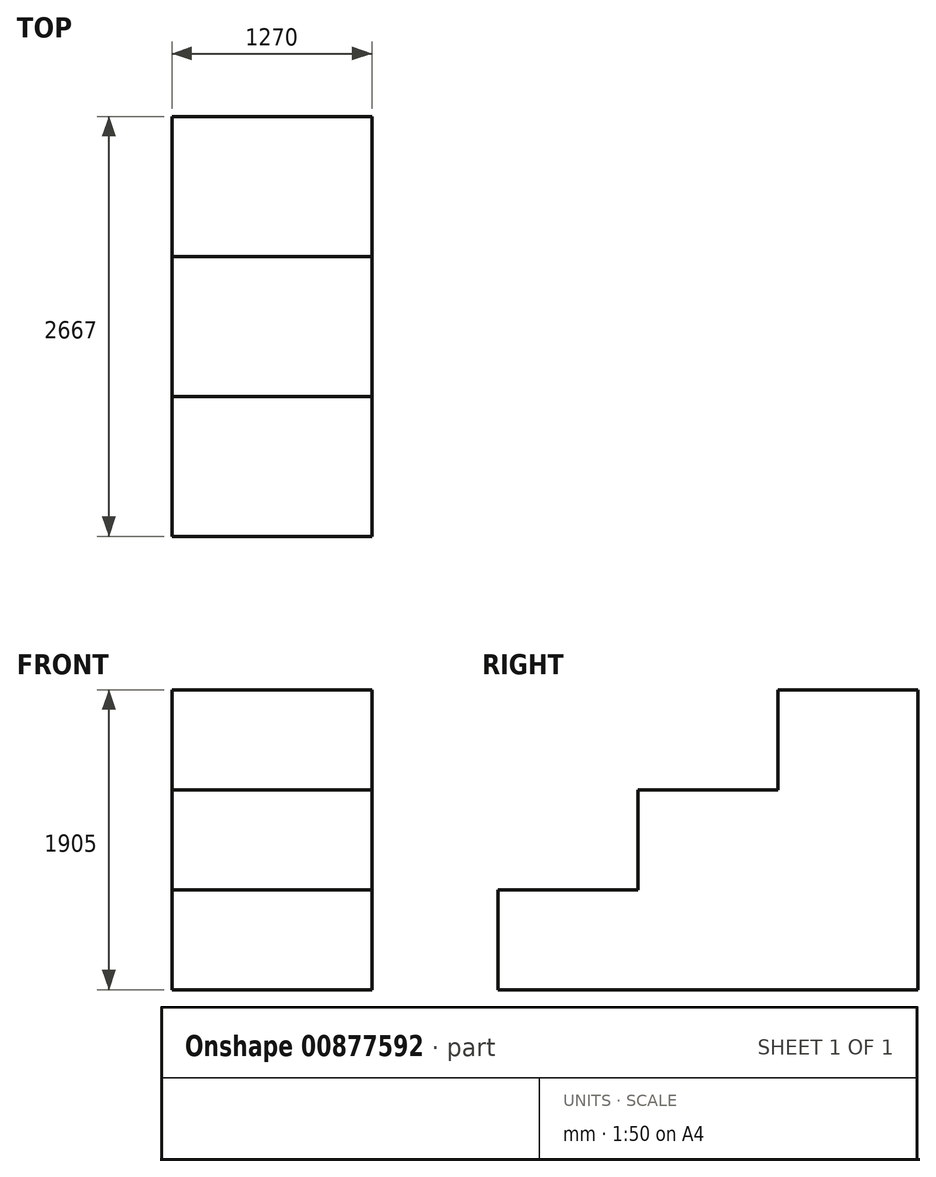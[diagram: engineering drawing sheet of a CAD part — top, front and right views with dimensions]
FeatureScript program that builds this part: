
annotation { "Feature Type Name" : "Feature", "Feature Type Description" : "" }
export const myFeature = defineFeature(function(context is Context, id is Id, definition is map)
    precondition{}
    {
        {
            var Q0;
            Q0=qCreatedBy(makeId("Right.planeOp"),FACE);
            var sketch = newSketch(context, id + "F0", { "sketchPlane" : qUnion([Q0])});
            skLineSegment(sketch, "E0", {"start": v(0, 0) * mm, "end": v(-1905, 0) * mm});
            skLineSegment(sketch, "E1", {"start": v(-1905, 0) * mm, "end": v(-1905, 635) * mm});
            skLineSegment(sketch, "E2", {"start": v(-1905, 635) * mm, "end": v(-1016, 635) * mm});
            skLineSegment(sketch, "E3", {"start": v(-1016, 635) * mm, "end": v(-1016, 1270) * mm});
            skLineSegment(sketch, "E4", {"start": v(-1016, 1270) * mm, "end": v(-127, 1270) * mm});
            skLineSegment(sketch, "E5", {"start": v(-127, 1270) * mm, "end": v(-127, 1905) * mm});
            skLineSegment(sketch, "E6", {"start": v(-127, 1905) * mm, "end": v(762, 1905) * mm});
            skLineSegment(sketch, "E7", {"start": v(762, 1905) * mm, "end": v(762, 0) * mm});
            skLineSegment(sketch, "E8", {"start": v(762, 0) * mm, "end": v(-1905, 0) * mm});
            skSolve(sketch);
        }
        {
            var Q0;
            {var subQ0=sQuery(id+"F0.wireOp",EDGE,"E1");Q0=makeQuery(id+"F0.imprint","IMPRINT",FACE,{"disambiguationData":[TD([[makeQuery(id+"F0.imprint","IMPRINT",EDGE,{"derivedFrom":subQ0}),-1.0]])]});}
            extrude(context, id + "F1", {"entities" : qUnion([Q0]), "oppositeDirection" : true, "depth" : 1270 * mm, "offsetDistance" : 25.4 * mm});
        }
    });
